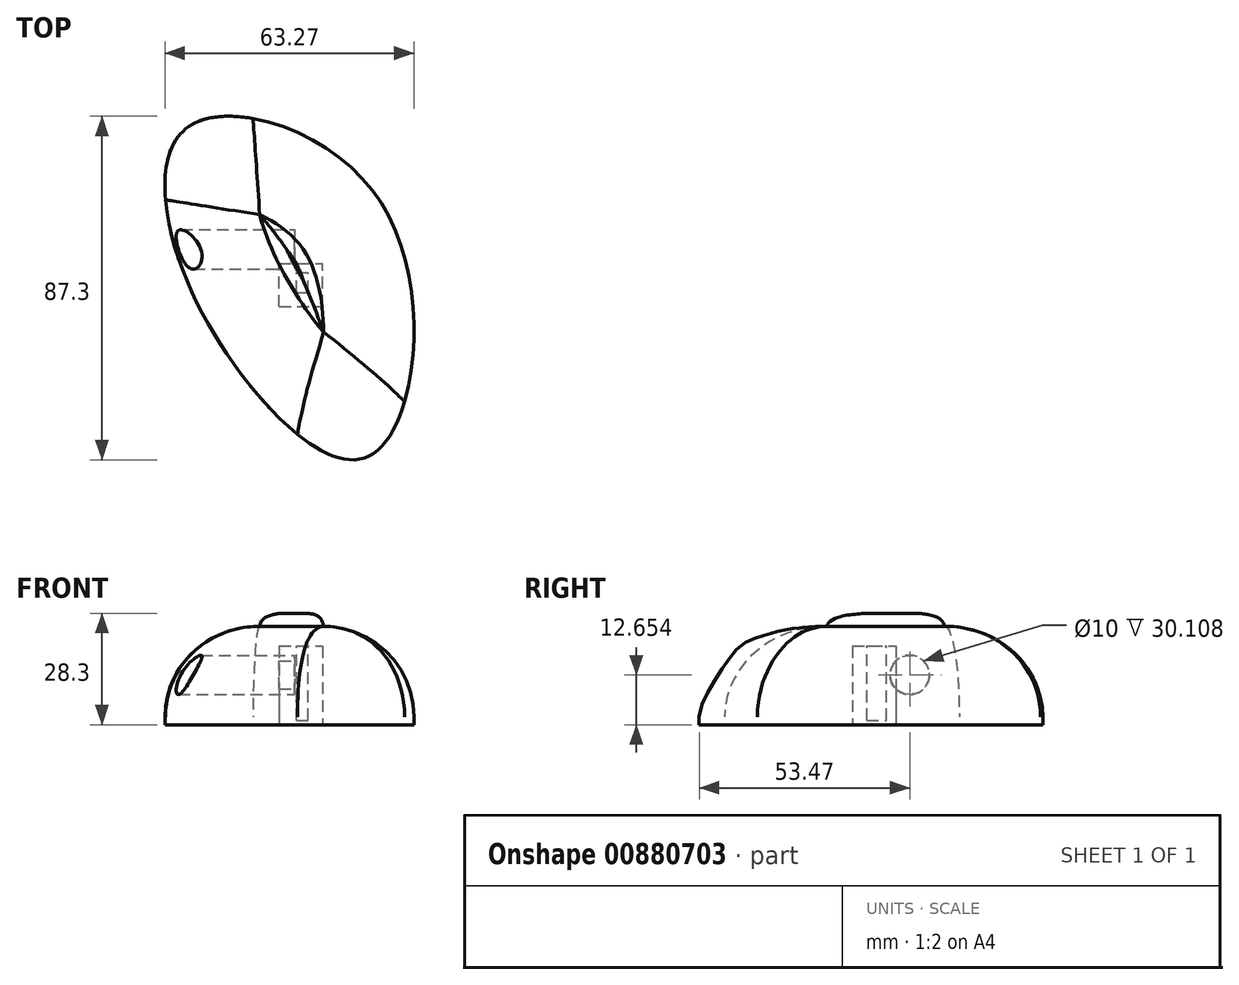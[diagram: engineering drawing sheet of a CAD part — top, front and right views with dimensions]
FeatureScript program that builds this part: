
annotation { "Feature Type Name" : "Feature", "Feature Type Description" : "" }
export const myFeature = defineFeature(function(context is Context, id is Id, definition is map)
    precondition{}
    {
        {
            var Q0;
            Q0=qCreatedBy(makeId("Top.planeOp"),FACE);
            var sketch = newSketch(context, id + "F0", { "sketchPlane" : qUnion([Q0])});
            skFitSpline(sketch, "E0", {"points": [v(-23.07, 37.2) * mm, v(-32.95, 21.12) * mm, v(-16.19, -23.88) * mm, v(19.17, -48.21) * mm, v(23.3, 13.78) * mm, v(-23.07, 37.2) * mm]});
            skSolve(sketch);
        }
        {
            var Q0;
            Q0=makeQuery(id+"F0.imprint","IMPRINT",FACE,{"disambiguationData":[TD([[makeQuery(id+"F0.imprint","IMPRINT",EDGE,{"derivedFrom":sQuery(id+"F0.wireOp",EDGE,"E0")}),1.0]])]});
            extrude(context, id + "F1", {"entities" : qUnion([Q0]), "depth" : 25 * mm, "offsetDistance" : 25.4 * mm});
        }
        {
            var Q0;
            Q0=makeQuery(id+"F1.opExtrude","CAP_FACE",FACE,{"disambiguationData":[OSD([sQuery(id+"F0.wireOp",EDGE,"E0")])],"isStart":false});
            fillet(context, id + "F2", {"entities" : qUnion([Q0]), "radius" : 23 * mm, "tangentPropagation" : true, "allowEdgeOverflow" : false});
        }
        {
            var Q0;
            Q0=makeQuery(id+"F1.opExtrude","CAP_FACE",FACE,{"disambiguationData":[OSD([sQuery(id+"F0.wireOp",EDGE,"E0")])],"isStart":false});
            extrude(context, id + "F3", {"entities" : qUnion([Q0]), "operationType" : NewBodyOperationType.ADD, "depth" : 3.3 * mm, "offsetDistance" : 25 * mm});
        }
        {
            var Q0;
            {var subQ0=sQuery(id+"F0.wireOp",EDGE,"E0");Q0=makeQuery(id+"F3.opExtrude","CAP_EDGE",EDGE,{"disambiguationData":[OSD([subQ0]),TDD([makeQuery(id+"F2.opFillet","BLEND_EDGE",EDGE,{"disambiguationData":[OD(1.0)],"blendedFrom":[makeQuery(id+"F1.opExtrude","CAP_EDGE",EDGE,{"disambiguationData":[OSD([subQ0])],"isStart":false}),makeQuery(id+"F1.opExtrude","CAP_FACE",FACE,{"disambiguationData":[OSD([subQ0])],"isStart":false})],"blendedInto":[makeQuery(id+"F1.opExtrude","CAP_FACE",FACE,{"disambiguationData":[OSD([subQ0])],"isStart":false})]})])],"isStart":false});}
            var Q1;
            {var subQ0=sQuery(id+"F0.wireOp",EDGE,"E0");Q1=makeQuery(id+"F3.opExtrude","CAP_EDGE",EDGE,{"disambiguationData":[OSD([subQ0]),TDD([makeQuery(id+"F2.opFillet","BLEND_EDGE",EDGE,{"disambiguationData":[OD(0.0)],"blendedFrom":[makeQuery(id+"F1.opExtrude","CAP_EDGE",EDGE,{"disambiguationData":[OSD([subQ0])],"isStart":false}),makeQuery(id+"F1.opExtrude","CAP_FACE",FACE,{"disambiguationData":[OSD([subQ0])],"isStart":false})],"blendedInto":[makeQuery(id+"F1.opExtrude","CAP_FACE",FACE,{"disambiguationData":[OSD([subQ0])],"isStart":false})]})])],"isStart":false});}
            fillet(context, id + "F4", {"entities" : qUnion([Q0, Q1]), "radius" : 3.4 * mm, "tangentPropagation" : true, "allowEdgeOverflow" : false});
        }
        {
            var Q0;
            Q0=makeQuery(id+"F1.opExtrude","CAP_FACE",FACE,{"disambiguationData":[OSD([sQuery(id+"F0.wireOp",EDGE,"E0")])],"isStart":true});
            var sketch = newSketch(context, id + "F5", { "sketchPlane" : qUnion([Q0])});
            skLineSegment(sketch, "E1.bottom", {"start": v(-3.93, 10.36) * mm, "end": v(7.07, 10.36) * mm});
            skLineSegment(sketch, "E1.top", {"start": v(-3.93, -0.64) * mm, "end": v(7.07, -0.64) * mm});
            skLineSegment(sketch, "E1.left", {"start": v(-3.93, 10.36) * mm, "end": v(-3.93, -0.64) * mm});
            skLineSegment(sketch, "E1.right", {"start": v(7.07, 10.36) * mm, "end": v(7.07, -0.64) * mm});
            skSolve(sketch);
        }
        {
            var Q0;
            Q0=makeQuery(id+"F5.imprint","IMPRINT",FACE,{"disambiguationData":[TD([[makeQuery(id+"F5.imprint","IMPRINT",EDGE,{"derivedFrom":sQuery(id+"F5.wireOp",EDGE,"E1.bottom")}),-1.0]])]});
            extrude(context, id + "F6", {"entities" : qUnion([Q0]), "operationType" : NewBodyOperationType.REMOVE, "oppositeDirection" : true, "depth" : 20 * mm, "offsetDistance" : 25 * mm});
        }
        {
            var Q0;
            Q0=makeQuery(id+"F6.boolean.opBoolean","COPY",FACE,{"derivedFrom":makeQuery(id+"F6.opExtrude","CAP_FACE",FACE,{"disambiguationData":[OSD([sQuery(id+"F5.wireOp",EDGE,"E1.bottom"),sQuery(id+"F5.wireOp",EDGE,"E1.top"),sQuery(id+"F5.wireOp",EDGE,"E1.left"),sQuery(id+"F5.wireOp",EDGE,"E1.right")])],"isStart":false})});
            var sketch = newSketch(context, id + "F7", { "sketchPlane" : qUnion([Q0])});
            skLineSegment(sketch, "E2.bottom", {"start": v(0.47, 6.73) * mm, "end": v(3.47, 6.73) * mm});
            skLineSegment(sketch, "E2.top", {"start": v(0.47, 1.73) * mm, "end": v(3.47, 1.73) * mm});
            skLineSegment(sketch, "E2.left", {"start": v(0.47, 6.73) * mm, "end": v(0.47, 1.73) * mm});
            skLineSegment(sketch, "E2.right", {"start": v(3.47, 6.73) * mm, "end": v(3.47, 1.73) * mm});
            skSolve(sketch);
        }
        {
            var Q0;
            Q0=makeQuery(id+"F7.imprint","IMPRINT",FACE,{"disambiguationData":[TD([[makeQuery(id+"F7.imprint","IMPRINT",EDGE,{"derivedFrom":sQuery(id+"F7.wireOp",EDGE,"E2.bottom")}),-1.0]])]});
            extrude(context, id + "F8", {"entities" : qUnion([Q0]), "operationType" : NewBodyOperationType.ADD, "depth" : 18.9 * mm, "offsetDistance" : 25 * mm});
        }
        {
            var Q0;
            Q0=qCreatedBy(makeId("Right.planeOp"),FACE);
            var sketch = newSketch(context, id + "F9", { "sketchPlane" : qUnion([Q0])});
            skCircle(sketch, "E3", {"center": v(4.18, 12.65) * mm, "radius": 5 * mm});
            skSolve(sketch);
        }
        {
            var Q0;
            Q0 = qSketchRegion(id + "F9", true);
            extrude(context, id + "F10", {"entities" : qUnion([Q0]), "operationType" : NewBodyOperationType.REMOVE, "oppositeDirection" : true, "depth" : 66.8 * mm, "offsetDistance" : 25 * mm});
        }
    });
